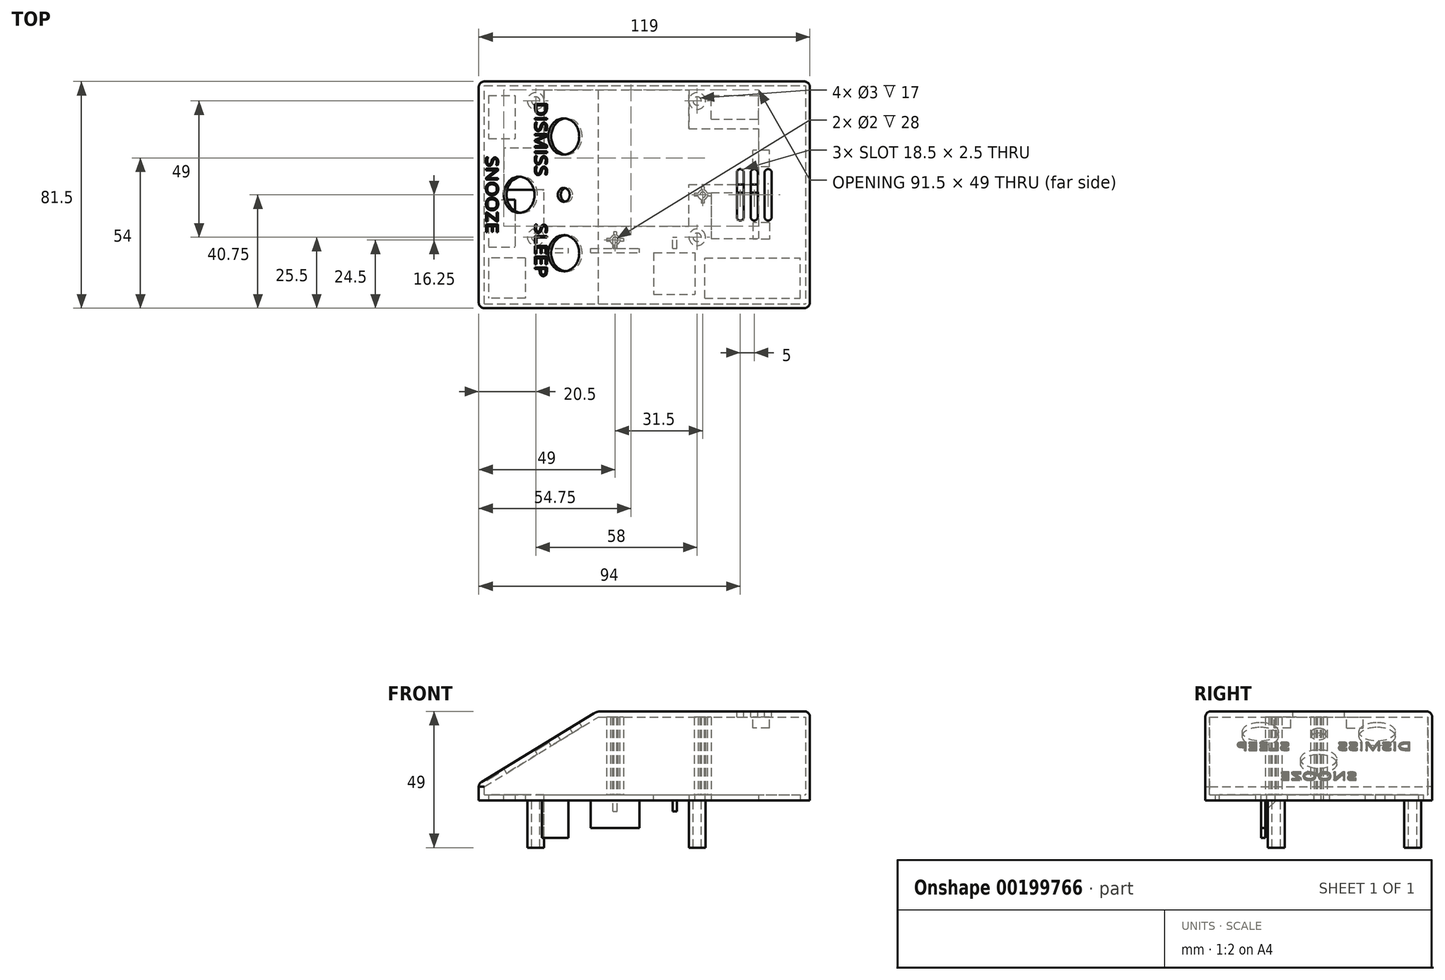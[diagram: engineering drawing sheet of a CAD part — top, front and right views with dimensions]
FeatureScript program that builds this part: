
annotation { "Feature Type Name" : "Feature", "Feature Type Description" : "" }
export const myFeature = defineFeature(function(context is Context, id is Id, definition is map)
    precondition{}
    {
        {
            var Q0;
            Q0=qCreatedBy(makeId("Top.planeOp"),FACE);
            var sketch = newSketch(context, id + "F0", { "sketchPlane" : qUnion([Q0])});
            skLineSegment(sketch, "E0.bottom", {"start": v(0, 0) * mm, "end": v(89, 0) * mm});
            skLineSegment(sketch, "E0.top", {"start": v(0, 60) * mm, "end": v(89, 60) * mm});
            skLineSegment(sketch, "E0.left", {"start": v(0, 0) * mm, "end": v(0, 60) * mm});
            skLineSegment(sketch, "E0.right", {"start": v(89, 0) * mm, "end": v(89, 60) * mm});
            skLineSegment(sketch, "E1", {"start": v(0, 60) * mm, "end": v(-15, 60) * mm});
            skLineSegment(sketch, "E2", {"start": v(-15, 60) * mm, "end": v(-15, 0) * mm});
            skLineSegment(sketch, "E3", {"start": v(-15, 0) * mm, "end": v(-15, -20) * mm});
            skLineSegment(sketch, "E4", {"start": v(-15, -20) * mm, "end": v(89, -20) * mm});
            skLineSegment(sketch, "E5", {"start": v(89, -20) * mm, "end": v(104, -20) * mm});
            skLineSegment(sketch, "E6", {"start": v(104, -20) * mm, "end": v(104, 60) * mm});
            skLineSegment(sketch, "E7", {"start": v(104, 60) * mm, "end": v(89, 60) * mm});
            skLineSegment(sketch, "E8.bottom", {"start": v(-15, 60) * mm, "end": v(104, 60) * mm});
            skLineSegment(sketch, "E8.top", {"start": v(-15, 61.5) * mm, "end": v(104, 61.5) * mm});
            skLineSegment(sketch, "E8.left", {"start": v(-15, 60) * mm, "end": v(-15, 61.5) * mm});
            skLineSegment(sketch, "E8.right", {"start": v(104, 60) * mm, "end": v(104, 61.5) * mm});
            skSolve(sketch);
        }
        {
            var Q0;
            Q0=makeQuery(id+"F0.imprint","IMPRINT",FACE,{"disambiguationData":[TD([[makeQuery(id+"F0.imprint","IMPRINT",EDGE,{"derivedFrom":sQuery(id+"F0.wireOp",EDGE,"E0.bottom")}),-1.0]])]});
            var Q1;
            Q1=makeQuery(id+"F0.imprint","IMPRINT",FACE,{"disambiguationData":[TD([[makeQuery(id+"F0.imprint","IMPRINT",EDGE,{"derivedFrom":sQuery(id+"F0.wireOp",EDGE,"E8.top")}),-1.0]])]});
            var Q2;
            Q2=makeQuery(id+"F0.imprint","IMPRINT",FACE,{"disambiguationData":[TD([[makeQuery(id+"F0.imprint","IMPRINT",EDGE,{"derivedFrom":sQuery(id+"F0.wireOp",EDGE,"E0.bottom")}),1.0]])]});
            extrude(context, id + "F1", {"entities" : qUnion([Q0, Q1, Q2]), "depth" : 2 * mm});
        }
        {
            var Q0;
            Q0=makeQuery(id+"F1.opExtrude","CAP_FACE",FACE,{"disambiguationData":[OSD([sQuery(id+"F0.wireOp",EDGE,"E2"),sQuery(id+"F0.wireOp",EDGE,"E3"),sQuery(id+"F0.wireOp",EDGE,"E4"),sQuery(id+"F0.wireOp",EDGE,"E5"),sQuery(id+"F0.wireOp",EDGE,"E6"),sQuery(id+"F0.wireOp",EDGE,"E8.top"),sQuery(id+"F0.wireOp",EDGE,"E8.left"),sQuery(id+"F0.wireOp",EDGE,"E8.right")])],"isStart":true});
            var sketch = newSketch(context, id + "F2", { "sketchPlane" : qUnion([Q0])});
            skCircle(sketch, "E9", {"center": v(5.5, -5.5) * mm, "radius": 1.5 * mm});
            skCircle(sketch, "E10.0", {"center": v(5.5, -5.5) * mm, "radius": 3 * mm});
            skCircle(sketch, "E11.0.1.0", {"center": v(5.5, -54.5) * mm, "radius": 3 * mm});
            skCircle(sketch, "E11.0.1.1", {"center": v(5.5, -54.5) * mm, "radius": 1.5 * mm});
            skCircle(sketch, "E11.1.0.0", {"center": v(63.5, -5.5) * mm, "radius": 3 * mm});
            skCircle(sketch, "E11.1.0.1", {"center": v(63.5, -5.5) * mm, "radius": 1.5 * mm});
            skCircle(sketch, "E11.1.1.0", {"center": v(63.5, -54.5) * mm, "radius": 3 * mm});
            skCircle(sketch, "E11.1.1.1", {"center": v(63.5, -54.5) * mm, "radius": 1.5 * mm});
            skLineSegment(sketch, "E11.direction1", {"start": v(5.5, -5.5) * mm, "end": v(63.5, -5.5) * mm, "construction": true});
            skLineSegment(sketch, "E11.direction2", {"start": v(5.5, -5.5) * mm, "end": v(5.5, -54.5) * mm, "construction": true});
            skSolve(sketch);
        }
        {
            var Q0;
            Q0=makeQuery(id+"F2.imprint","IMPRINT",FACE,{"disambiguationData":[TD([[makeQuery(id+"F2.imprint","IMPRINT",EDGE,{"derivedFrom":sQuery(id+"F2.wireOp",EDGE,"E9")}),-1.0]])]});
            var Q1;
            Q1=makeQuery(id+"F2.imprint","IMPRINT",FACE,{"disambiguationData":[TD([[makeQuery(id+"F2.imprint","IMPRINT",EDGE,{"derivedFrom":sQuery(id+"F2.wireOp",EDGE,"E11.1.0.0")}),1.0]])]});
            var Q2;
            Q2=makeQuery(id+"F2.imprint","IMPRINT",FACE,{"disambiguationData":[TD([[makeQuery(id+"F2.imprint","IMPRINT",EDGE,{"derivedFrom":sQuery(id+"F2.wireOp",EDGE,"E11.0.1.0")}),1.0]])]});
            var Q3;
            Q3=makeQuery(id+"F2.imprint","IMPRINT",FACE,{"disambiguationData":[TD([[makeQuery(id+"F2.imprint","IMPRINT",EDGE,{"derivedFrom":sQuery(id+"F2.wireOp",EDGE,"E11.1.1.0")}),1.0]])]});
            extrude(context, id + "F3", {"entities" : qUnion([Q0, Q1, Q2, Q3]), "operationType" : NewBodyOperationType.ADD, "depth" : 17 * mm});
        }
        {
            var Q0;
            Q0=makeQuery(id+"F1.opExtrude","CAP_FACE",FACE,{"disambiguationData":[OSD([sQuery(id+"F0.wireOp",EDGE,"E2"),sQuery(id+"F0.wireOp",EDGE,"E3"),sQuery(id+"F0.wireOp",EDGE,"E4"),sQuery(id+"F0.wireOp",EDGE,"E5"),sQuery(id+"F0.wireOp",EDGE,"E6"),sQuery(id+"F0.wireOp",EDGE,"E8.top"),sQuery(id+"F0.wireOp",EDGE,"E8.left"),sQuery(id+"F0.wireOp",EDGE,"E8.right")])],"isStart":false});
            var sketch = newSketch(context, id + "F4", { "sketchPlane" : qUnion([Q0])});
            skLineSegment(sketch, "E12.bottom", {"start": v(8.5, 9.5) * mm, "end": v(60.5, 9.5) * mm});
            skLineSegment(sketch, "E12.top", {"start": v(8.5, 58.5) * mm, "end": v(60.5, 58.5) * mm});
            skLineSegment(sketch, "E12.left", {"start": v(8.5, 9.5) * mm, "end": v(8.5, 58.5) * mm});
            skLineSegment(sketch, "E12.right", {"start": v(60.5, 9.5) * mm, "end": v(60.5, 58.5) * mm});
            skLineSegment(sketch, "E13.bottom", {"start": v(0, 0) * mm, "end": v(89, 0) * mm});
            skLineSegment(sketch, "E13.top", {"start": v(0, 60) * mm, "end": v(89, 60) * mm});
            skLineSegment(sketch, "E13.left", {"start": v(0, 0) * mm, "end": v(0, 60) * mm});
            skLineSegment(sketch, "E13.right", {"start": v(89, 0) * mm, "end": v(89, 60) * mm});
            skSolve(sketch);
        }
        {
            var Q0;
            Q0=makeQuery(id+"F4.imprint","IMPRINT",FACE,{"disambiguationData":[TD([[makeQuery(id+"F4.imprint","IMPRINT",EDGE,{"derivedFrom":sQuery(id+"F4.wireOp",EDGE,"E12.bottom")}),1.0]])]});
            var Q1;
            {var subQ0=sQuery(id+"F0.wireOp",EDGE,"E8.top");var subQ1=sQuery(id+"F0.wireOp",EDGE,"E8.right");var subQ2=sQuery(id+"F0.wireOp",EDGE,"E6");var subQ3=sQuery(id+"F0.wireOp",EDGE,"E5");var subQ4=sQuery(id+"F0.wireOp",EDGE,"E4");var subQ5=sQuery(id+"F0.wireOp",EDGE,"E8.left");var subQ6=sQuery(id+"F0.wireOp",EDGE,"E3");var subQ7=sQuery(id+"F0.wireOp",EDGE,"E2");Q1=makeQuery(id+"F3.boolean.opBoolean","SPLIT",FACE,{"disambiguationData":[TD([makeQuery(id+"F1.opExtrude","SWEPT_FACE",FACE,{"disambiguationData":[OSD([subQ0])]})])],"derivedFrom":makeQuery(id+"F1.opExtrude","CAP_FACE",FACE,{"disambiguationData":[OSD([subQ7,subQ6,subQ4,subQ3,subQ2,subQ0,subQ5,subQ1])],"isStart":true})});}
            extrude(context, id + "F5", {"entities" : qUnion([Q0]), "operationType" : NewBodyOperationType.REMOVE, "endBound" : BoundingType.UP_TO_SURFACE, "oppositeDirection" : true, "endBoundEntityFace" : qUnion([Q1]), "depth" : 25 * mm});
        }
        {
            var Q0;
            Q0=makeQuery(id+"F1.opExtrude","CAP_FACE",FACE,{"disambiguationData":[OSD([sQuery(id+"F0.wireOp",EDGE,"E2"),sQuery(id+"F0.wireOp",EDGE,"E3"),sQuery(id+"F0.wireOp",EDGE,"E4"),sQuery(id+"F0.wireOp",EDGE,"E5"),sQuery(id+"F0.wireOp",EDGE,"E6"),sQuery(id+"F0.wireOp",EDGE,"E8.top"),sQuery(id+"F0.wireOp",EDGE,"E8.left"),sQuery(id+"F0.wireOp",EDGE,"E8.right")])],"isStart":false});
            var sketch = newSketch(context, id + "F6", { "sketchPlane" : qUnion([Q0])});
            skLineSegment(sketch, "E14.bottom", {"start": v(104, 61.5) * mm, "end": v(102.5, 61.5) * mm});
            skLineSegment(sketch, "E14.top", {"start": v(104, -20) * mm, "end": v(102.5, -20) * mm});
            skLineSegment(sketch, "E14.left", {"start": v(104, 61.5) * mm, "end": v(104, -20) * mm});
            skLineSegment(sketch, "E14.right", {"start": v(102.5, 61.5) * mm, "end": v(102.5, -20) * mm});
            skSolve(sketch);
        }
        {
            var Q0;
            Q0=makeQuery(id+"F6.imprint","IMPRINT",FACE,{"disambiguationData":[TD([[makeQuery(id+"F6.imprint","IMPRINT",EDGE,{"derivedFrom":sQuery(id+"F6.wireOp",EDGE,"E14.bottom")}),-1.0]])]});
            extrude(context, id + "F7", {"entities" : qUnion([Q0]), "operationType" : NewBodyOperationType.ADD, "depth" : 30 * mm});
        }
        {
            var Q0;
            Q0=makeQuery(id+"F1.opExtrude","CAP_FACE",FACE,{"disambiguationData":[OSD([sQuery(id+"F0.wireOp",EDGE,"E2"),sQuery(id+"F0.wireOp",EDGE,"E3"),sQuery(id+"F0.wireOp",EDGE,"E4"),sQuery(id+"F0.wireOp",EDGE,"E5"),sQuery(id+"F0.wireOp",EDGE,"E6"),sQuery(id+"F0.wireOp",EDGE,"E8.top"),sQuery(id+"F0.wireOp",EDGE,"E8.left"),sQuery(id+"F0.wireOp",EDGE,"E8.right")])],"isStart":false});
            var sketch = newSketch(context, id + "F8", { "sketchPlane" : qUnion([Q0])});
            skLineSegment(sketch, "E15.bottom", {"start": v(8.5, 37.5) * mm, "end": v(-6, 37.5) * mm});
            skLineSegment(sketch, "E15.top", {"start": v(8.5, 22.5) * mm, "end": v(-6, 22.5) * mm});
            skLineSegment(sketch, "E15.left", {"start": v(8.5, 37.5) * mm, "end": v(8.5, 22.5) * mm});
            skLineSegment(sketch, "E15.right", {"start": v(-6, 37.5) * mm, "end": v(-6, 22.5) * mm});
            skLineSegment(sketch, "E16.bottom", {"start": v(8.5, 22.5) * mm, "end": v(1.5, 22.5) * mm});
            skLineSegment(sketch, "E16.top", {"start": v(8.5, 9.5) * mm, "end": v(1.5, 9.5) * mm});
            skLineSegment(sketch, "E16.left", {"start": v(8.5, 22.5) * mm, "end": v(8.5, 9.5) * mm});
            skLineSegment(sketch, "E16.right", {"start": v(1.5, 22.5) * mm, "end": v(1.5, 9.5) * mm});
            skSolve(sketch);
        }
        {
            var Q0;
            Q0=makeQuery(id+"F8.imprint","IMPRINT",FACE,{"disambiguationData":[TD([[makeQuery(id+"F8.imprint","IMPRINT",EDGE,{"derivedFrom":sQuery(id+"F8.wireOp",EDGE,"E15.bottom")}),1.0]])]});
            var Q1;
            Q1=makeQuery(id+"F8.imprint","IMPRINT",FACE,{"disambiguationData":[TD([[makeQuery(id+"F8.imprint","IMPRINT",EDGE,{"derivedFrom":sQuery(id+"F8.wireOp",EDGE,"E16.bottom")}),1.0]])]});
            var Q2;
            {var subQ0=sQuery(id+"F0.wireOp",EDGE,"E8.top");var subQ1=sQuery(id+"F0.wireOp",EDGE,"E8.right");var subQ2=sQuery(id+"F0.wireOp",EDGE,"E6");var subQ3=sQuery(id+"F0.wireOp",EDGE,"E5");var subQ4=sQuery(id+"F0.wireOp",EDGE,"E4");var subQ5=sQuery(id+"F0.wireOp",EDGE,"E8.left");var subQ6=sQuery(id+"F0.wireOp",EDGE,"E3");var subQ7=sQuery(id+"F0.wireOp",EDGE,"E2");Q2=makeQuery(id+"F3.boolean.opBoolean","SPLIT",FACE,{"disambiguationData":[TD([makeQuery(id+"F1.opExtrude","SWEPT_FACE",FACE,{"disambiguationData":[OSD([subQ0])]})])],"derivedFrom":makeQuery(id+"F1.opExtrude","CAP_FACE",FACE,{"disambiguationData":[OSD([subQ7,subQ6,subQ4,subQ3,subQ2,subQ0,subQ5,subQ1])],"isStart":true})});}
            extrude(context, id + "F9", {"entities" : qUnion([Q0, Q1]), "operationType" : NewBodyOperationType.REMOVE, "endBound" : BoundingType.UP_TO_SURFACE, "oppositeDirection" : true, "endBoundEntityFace" : qUnion([Q2]), "depth" : 25 * mm});
        }
        {
            var Q0;
            Q0=makeQuery(id+"F7.boolean.opBoolean","MERGE",FACE,{"derivedFrom":[makeQuery(id+"F1.opExtrude","SWEPT_FACE",FACE,{"disambiguationData":[OSD([sQuery(id+"F0.wireOp",EDGE,"E8.top")])]}),makeQuery(id+"F7.opExtrude","SWEPT_FACE",FACE,{"disambiguationData":[OSD([sQuery(id+"F6.wireOp",EDGE,"E14.bottom")])]})]});
            var sketch = newSketch(context, id + "F10", { "sketchPlane" : qUnion([Q0])});
            skLineSegment(sketch, "E17", {"start": v(15, 2) * mm, "end": v(15, 6) * mm});
            skLineSegment(sketch, "E18", {"start": v(15, 6) * mm, "end": v(-27.5, 32) * mm});
            skLineSegment(sketch, "E19", {"start": v(-27.5, 32) * mm, "end": v(-102.5, 32) * mm});
            skSolve(sketch);
        }
        {
            var Q0;
            Q0=makeQuery(id+"F10.imprint","IMPRINT",FACE,{"disambiguationData":[TD([[makeQuery(id+"F10.imprint","IMPRINT",EDGE,{"derivedFrom":sQuery(id+"F10.wireOp",EDGE,"E17")}),1.0]])]});
            extrude(context, id + "F11", {"entities" : qUnion([Q0]), "operationType" : NewBodyOperationType.ADD, "oppositeDirection" : true, "depth" : 1.5 * mm});
        }
        {
            var Q0;
            Q0=makeQuery(id+"F7.boolean.opBoolean","MERGE",FACE,{"derivedFrom":[makeQuery(id+"F1.opExtrude","SWEPT_FACE",FACE,{"disambiguationData":[OSD([sQuery(id+"F0.wireOp",EDGE,"E4"),sQuery(id+"F0.wireOp",EDGE,"E5")])]}),makeQuery(id+"F7.opExtrude","SWEPT_FACE",FACE,{"disambiguationData":[OSD([sQuery(id+"F6.wireOp",EDGE,"E14.top")])]})]});
            var sketch = newSketch(context, id + "F12", { "sketchPlane" : qUnion([Q0])});
            skLineSegment(sketch, "E20.0.0", {"start": v(104, 0) * mm, "end": v(-15, 0) * mm});
            skLineSegment(sketch, "E20.0.1", {"start": v(-15, 0) * mm, "end": v(-15, 6) * mm});
            skLineSegment(sketch, "E20.0.2", {"start": v(-15, 6) * mm, "end": v(27.5, 32) * mm});
            skLineSegment(sketch, "E20.0.3", {"start": v(27.5, 32) * mm, "end": v(104, 32) * mm});
            skLineSegment(sketch, "E20.0.4", {"start": v(104, 32) * mm, "end": v(104, 0) * mm});
            skSolve(sketch);
        }
        {
            var Q0;
            {var subQ4=sQuery(id+"F12.wireOp",EDGE,"E20.0.2");Q0=makeQuery(id+"F12.imprint","IMPRINT",FACE,{"disambiguationData":[TD([[makeQuery(id+"F12.imprint","IMPRINT",EDGE,{"derivedFrom":subQ4}),-1.0]])]});}
            extrude(context, id + "F13", {"entities" : qUnion([Q0]), "operationType" : NewBodyOperationType.ADD, "oppositeDirection" : true, "depth" : 1.5 * mm});
        }
        {
            var Q0;
            Q0=makeQuery(id+"F1.opExtrude","CAP_FACE",FACE,{"disambiguationData":[OSD([sQuery(id+"F0.wireOp",EDGE,"E2"),sQuery(id+"F0.wireOp",EDGE,"E3"),sQuery(id+"F0.wireOp",EDGE,"E4"),sQuery(id+"F0.wireOp",EDGE,"E5"),sQuery(id+"F0.wireOp",EDGE,"E6"),sQuery(id+"F0.wireOp",EDGE,"E8.top"),sQuery(id+"F0.wireOp",EDGE,"E8.left"),sQuery(id+"F0.wireOp",EDGE,"E8.right")])],"isStart":false});
            var sketch = newSketch(context, id + "F14", { "sketchPlane" : qUnion([Q0])});
            skLineSegment(sketch, "E21.bottom", {"start": v(47.88, 0) * mm, "end": v(62.69, 0) * mm});
            skLineSegment(sketch, "E21.top", {"start": v(47.88, -15) * mm, "end": v(62.69, -15) * mm});
            skLineSegment(sketch, "E21.left", {"start": v(47.88, 0) * mm, "end": v(47.88, -15) * mm});
            skLineSegment(sketch, "E21.right", {"start": v(62.69, 0) * mm, "end": v(62.69, -15) * mm});
            skSolve(sketch);
        }
        {
            var Q0;
            Q0=makeQuery(id+"F14.imprint","IMPRINT",FACE,{"disambiguationData":[TD([[makeQuery(id+"F14.imprint","IMPRINT",EDGE,{"derivedFrom":sQuery(id+"F14.wireOp",EDGE,"E21.bottom")}),-1.0]])]});
            extrude(context, id + "F15", {"entities" : qUnion([Q0]), "operationType" : NewBodyOperationType.REMOVE, "endBound" : BoundingType.UP_TO_NEXT, "oppositeDirection" : true, "depth" : 25 * mm});
        }
        {
            var Q0;
            Q0=makeQuery(id+"F11.opExtrude","CAP_FACE",FACE,{"disambiguationData":[OSD([sQuery(id+"F0.wireOp",EDGE,"E8.top"),sQuery(id+"F6.wireOp",EDGE,"E14.bottom"),sQuery(id+"F6.wireOp",EDGE,"E14.right"),sQuery(id+"F10.wireOp",EDGE,"E17"),sQuery(id+"F10.wireOp",EDGE,"E18"),sQuery(id+"F10.wireOp",EDGE,"E19")])],"isStart":false});
            var sketch = newSketch(context, id + "F16", { "sketchPlane" : qUnion([Q0])});
            skLineSegment(sketch, "E22", {"start": v(-13, 2) * mm, "end": v(-13, 4.88) * mm});
            skLineSegment(sketch, "E23", {"start": v(-13, 4.88) * mm, "end": v(28.06, 30) * mm});
            skLineSegment(sketch, "E24", {"start": v(28.06, 30) * mm, "end": v(102.5, 30) * mm});
            skSolve(sketch);
        }
        {
            var Q0;
            {var subQ5=sQuery(id+"F16.wireOp",EDGE,"E22");Q0=makeQuery(id+"F16.imprint","IMPRINT",FACE,{"disambiguationData":[TD([[makeQuery(id+"F16.imprint","IMPRINT",EDGE,{"derivedFrom":subQ5}),1.0]])]});}
            var Q1;
            Q1=makeQuery(id+"F13.opExtrude","CAP_FACE",FACE,{"disambiguationData":[OSD([sQuery(id+"F0.wireOp",EDGE,"E4"),sQuery(id+"F0.wireOp",EDGE,"E5"),sQuery(id+"F6.wireOp",EDGE,"E14.top"),sQuery(id+"F6.wireOp",EDGE,"E14.right"),sQuery(id+"F12.wireOp",EDGE,"E20.0.1"),sQuery(id+"F12.wireOp",EDGE,"E20.0.2"),sQuery(id+"F12.wireOp",EDGE,"E20.0.3")])],"isStart":false});
            extrude(context, id + "F17", {"entities" : qUnion([Q0]), "operationType" : NewBodyOperationType.ADD, "endBound" : BoundingType.UP_TO_SURFACE, "endBoundEntityFace" : qUnion([Q1]), "depth" : 25 * mm});
        }
        {
            var Q0;
            {var subQ0=sQuery(id+"F10.wireOp",EDGE,"E18");Q0=makeQuery(id+"F17.boolean.opBoolean","MERGE",FACE,{"derivedFrom":[makeQuery(id+"F11.opExtrude","SWEPT_FACE",FACE,{"disambiguationData":[OSD([subQ0])]}),makeQuery(id+"F13.opExtrude","SWEPT_FACE",FACE,{"disambiguationData":[OSD([sQuery(id+"F12.wireOp",EDGE,"E20.0.2")])]}),makeQuery(id+"F17.opExtrude","SWEPT_FACE",FACE,{"disambiguationData":[OSD([subQ0])]})]});}
            var sketch = newSketch(context, id + "F18", { "sketchPlane" : qUnion([Q0])});
            skCircle(sketch, "E25", {"center": v(7.34, 20.75) * mm, "radius": 6.5 * mm});
            skPoint(sketch, "E25.centerSnap0", {"position": v(-9.66, 20.75) * mm});
            skCircle(sketch, "E26", {"center": v(26.16, -0.25) * mm, "radius": 6.5 * mm});
            skCircle(sketch, "E27", {"center": v(26.16, 41.75) * mm, "radius": 6.5 * mm});
            skLineSegment(sketch, "E28", {"start": v(26.16, 41.75) * mm, "end": v(40.16, 41.75) * mm});
            skLineSegment(sketch, "E29", {"start": v(26.16, -0.25) * mm, "end": v(40.16, -0.25) * mm});
            skLineSegment(sketch, "E30", {"start": v(40.16, 41.75) * mm, "end": v(40.16, 20.75) * mm});
            skLineSegment(sketch, "E31", {"start": v(40.16, 20.75) * mm, "end": v(40.16, -0.25) * mm});
            skSolve(sketch);
        }
        {
            var Q0;
            Q0=makeQuery(id+"F18.imprint","IMPRINT",FACE,{"disambiguationData":[TD([[makeQuery(id+"F18.imprint","IMPRINT",EDGE,{"derivedFrom":sQuery(id+"F18.wireOp",EDGE,"E25")}),1.0]])]});
            var Q1;
            Q1=makeQuery(id+"F18.imprint","IMPRINT",FACE,{"disambiguationData":[TD([[makeQuery(id+"F18.imprint","IMPRINT",EDGE,{"derivedFrom":sQuery(id+"F18.wireOp",EDGE,"E27")}),1.0]])]});
            var Q2;
            Q2=makeQuery(id+"F18.imprint","IMPRINT",FACE,{"disambiguationData":[TD([[makeQuery(id+"F18.imprint","IMPRINT",EDGE,{"derivedFrom":sQuery(id+"F18.wireOp",EDGE,"E26")}),1.0]])]});
            extrude(context, id + "F19", {"entities" : qUnion([Q0, Q1, Q2]), "operationType" : NewBodyOperationType.REMOVE, "endBound" : BoundingType.UP_TO_NEXT, "oppositeDirection" : true, "depth" : 25 * mm});
        }
        {
            var Q0;
            {var subQ0=sQuery(id+"F10.wireOp",EDGE,"E18");Q0=makeQuery(id+"F17.boolean.opBoolean","MERGE",FACE,{"derivedFrom":[makeQuery(id+"F11.opExtrude","SWEPT_FACE",FACE,{"disambiguationData":[OSD([subQ0])]}),makeQuery(id+"F13.opExtrude","SWEPT_FACE",FACE,{"disambiguationData":[OSD([sQuery(id+"F12.wireOp",EDGE,"E20.0.2")])]}),makeQuery(id+"F17.opExtrude","SWEPT_FACE",FACE,{"disambiguationData":[OSD([subQ0])]})]});}
            var sketch = newSketch(context, id + "F20", { "sketchPlane" : qUnion([Q0])});
            skCircle(sketch, "E32.0", {"center": v(26.16, 41.75) * mm, "radius": 6.5 * mm});
            skCircle(sketch, "E33.0", {"center": v(26.16, -0.25) * mm, "radius": 6.5 * mm});
            skCircle(sketch, "E34.0", {"center": v(7.34, 20.75) * mm, "radius": 6.5 * mm});
            skCircle(sketch, "E35", {"center": v(26.16, 20.75) * mm, "radius": 2.5 * mm});
            skSolve(sketch);
        }
        {
            var Q0;
            Q0=makeQuery(id+"F20.imprint","IMPRINT",FACE,{"disambiguationData":[TD([[makeQuery(id+"F20.imprint","IMPRINT",EDGE,{"derivedFrom":sQuery(id+"F20.wireOp",EDGE,"E35")}),1.0]])]});
            extrude(context, id + "F21", {"entities" : qUnion([Q0]), "operationType" : NewBodyOperationType.REMOVE, "endBound" : BoundingType.UP_TO_NEXT, "oppositeDirection" : true, "depth" : 25 * mm});
        }
        {
            var Q0;
            {var subQ0=sQuery(id+"F10.wireOp",EDGE,"E18");Q0=makeQuery(id+"F17.boolean.opBoolean","MERGE",FACE,{"derivedFrom":[makeQuery(id+"F11.opExtrude","SWEPT_FACE",FACE,{"disambiguationData":[OSD([subQ0])]}),makeQuery(id+"F13.opExtrude","SWEPT_FACE",FACE,{"disambiguationData":[OSD([sQuery(id+"F12.wireOp",EDGE,"E20.0.2")])]}),makeQuery(id+"F17.opExtrude","SWEPT_FACE",FACE,{"disambiguationData":[OSD([subQ0])]})]});}
            var sketch = newSketch(context, id + "F22", { "sketchPlane" : qUnion([Q0])});
            skText(sketch, "E36", { "text": "SNOOZE", "fontName": "OpenSans-Regular.ttf"});
            skLineSegment(sketch, "E37", {"start": v(-7.16, 34.61) * mm, "end": v(-7.16, 61.5) * mm});
            skLineSegment(sketch, "E38", {"start": v(-7.16, 6.89) * mm, "end": v(-7.16, -20) * mm});
            skLineSegment(sketch, "E39", {"start": v(7.34, 20.75) * mm, "end": v(0.34, 20.75) * mm});
            skLineSegment(sketch, "E40", {"start": v(-2.16, 20.75) * mm, "end": v(0.34, 20.75) * mm});
            skLineSegment(sketch, "E41", {"start": v(-7.16, 20.75) * mm, "end": v(-9.66, 20.75) * mm});
            skText(sketch, "E42", { "text": "DISMISS\n", "fontName": "OpenSans-Regular.ttf"});
            skLineSegment(sketch, "E43", {"start": v(26.16, 41.75) * mm, "end": v(19.16, 41.75) * mm});
            skLineSegment(sketch, "E44", {"start": v(17.16, 41.75) * mm, "end": v(19.16, 41.75) * mm});
            skText(sketch, "E45", { "text": "SLEEP", "fontName": "OpenSans-Regular.ttf"});
            skLineSegment(sketch, "E46", {"start": v(26.16, -0.25) * mm, "end": v(19.16, -0.25) * mm});
            skLineSegment(sketch, "E47", {"start": v(17.16, -0.25) * mm, "end": v(19.16, -0.25) * mm});
            const initialGuessF22  = {"E36": [-0.00658, 0.03461, 0, -1, 0.005], "E42": [0.01402, 0.05413, 0, -1, 0.005], "E45": [0.01402, 0.01046, 0, -1, 0.005]};
            skSetInitialGuess(sketch, initialGuessF22);
            skSolve(sketch);
        }
        {
            var Q0;
            Q0=qSketchRegion(id+"F22",true);
            extrude(context, id + "F23", {"entities" : qUnion([Q0]), "operationType" : NewBodyOperationType.REMOVE, "oppositeDirection" : true, "depth" : 0.5 * mm});
        }
        {
            var Q0;
            {var subQ0=sQuery(id+"F10.wireOp",EDGE,"E19");var subQ1=sQuery(id+"F10.wireOp",EDGE,"E18");Q0=makeQuery(id+"F17.boolean.opBoolean","MERGE",EDGE,{"derivedFrom":[makeQuery(id+"F11.opExtrude","SWEPT_EDGE",EDGE,{"disambiguationData":[OSD([subQ1,subQ0])]}),makeQuery(id+"F13.opExtrude","SWEPT_EDGE",EDGE,{"disambiguationData":[OSD([sQuery(id+"F12.wireOp",EDGE,"E20.0.2"),sQuery(id+"F12.wireOp",EDGE,"E20.0.3")])]}),makeQuery(id+"F17.opExtrude","SWEPT_EDGE",EDGE,{"disambiguationData":[OSD([subQ1,subQ0])]})]});}
            fillet(context, id + "F24", {"entities" : qUnion([Q0]), "radius" : 5 * mm, "tangentPropagation" : true, "allowEdgeOverflow" : false});
        }
        {
            var Q0;
            {var subQ0=sQuery(id+"F10.wireOp",EDGE,"E19");Q0=makeQuery(id+"F17.boolean.opBoolean","MERGE",FACE,{"derivedFrom":[makeQuery(id+"F13.boolean.opBoolean","MERGE",FACE,{"derivedFrom":[makeQuery(id+"F11.boolean.opBoolean","MERGE",FACE,{"derivedFrom":[makeQuery(id+"F7.opExtrude","CAP_FACE",FACE,{"disambiguationData":[OSD([sQuery(id+"F6.wireOp",EDGE,"E14.bottom"),sQuery(id+"F6.wireOp",EDGE,"E14.top"),sQuery(id+"F6.wireOp",EDGE,"E14.left"),sQuery(id+"F6.wireOp",EDGE,"E14.right")])],"isStart":false}),makeQuery(id+"F11.opExtrude","SWEPT_FACE",FACE,{"disambiguationData":[OSD([subQ0])]})]}),makeQuery(id+"F13.opExtrude","SWEPT_FACE",FACE,{"disambiguationData":[OSD([sQuery(id+"F12.wireOp",EDGE,"E20.0.3")])]})]}),makeQuery(id+"F17.opExtrude","SWEPT_FACE",FACE,{"disambiguationData":[OSD([subQ0])]})]});}
            var sketch = newSketch(context, id + "F25", { "sketchPlane" : qUnion([Q0])});
            skLineSegment(sketch, "E48", {"start": v(79, 28.75) * mm, "end": v(79, 12.75) * mm});
            skLineSegment(sketch, "E49", {"start": v(79, 28.75) * mm, "end": v(79, 61.5) * mm});
            skLineSegment(sketch, "E50", {"start": v(79, 12.75) * mm, "end": v(79, -20) * mm});
            skArc(sketch, "E51.0.startCap", {"start": v(77.75, 28.75) * mm, "mid": v(79, 30) * mm, "end": v(80.25, 28.75) * mm});
            skArc(sketch, "E51.0.endCap", {"start": v(80.25, 12.75) * mm, "mid": v(79, 11.5) * mm, "end": v(77.75, 12.75) * mm});
            skLineSegment(sketch, "E51.0.left", {"start": v(80.25, 28.75) * mm, "end": v(80.25, 12.75) * mm});
            skLineSegment(sketch, "E51.0.right", {"start": v(77.75, 28.75) * mm, "end": v(77.75, 12.75) * mm});
            skLineSegment(sketch, "E52.1.0.0", {"start": v(85.25, 28.75) * mm, "end": v(85.25, 12.75) * mm});
            skLineSegment(sketch, "E52.1.0.1", {"start": v(82.75, 28.75) * mm, "end": v(82.75, 12.75) * mm});
            skArc(sketch, "E52.1.0.2", {"start": v(82.75, 28.75) * mm, "mid": v(84, 30) * mm, "end": v(85.25, 28.75) * mm});
            skArc(sketch, "E52.1.0.3", {"start": v(85.25, 12.75) * mm, "mid": v(84, 11.5) * mm, "end": v(82.75, 12.75) * mm});
            skLineSegment(sketch, "E52.2.0.0", {"start": v(90.25, 28.75) * mm, "end": v(90.25, 12.75) * mm});
            skLineSegment(sketch, "E52.2.0.1", {"start": v(87.75, 28.75) * mm, "end": v(87.75, 12.75) * mm});
            skArc(sketch, "E52.2.0.2", {"start": v(87.75, 28.75) * mm, "mid": v(89, 30) * mm, "end": v(90.25, 28.75) * mm});
            skArc(sketch, "E52.2.0.3", {"start": v(90.25, 12.75) * mm, "mid": v(89, 11.5) * mm, "end": v(87.75, 12.75) * mm});
            skLineSegment(sketch, "E52.direction1", {"start": v(80.25, 12.75) * mm, "end": v(85.25, 12.75) * mm, "construction": true});
            skSolve(sketch);
        }
        {
            var Q0;
            {var subQ1=sQuery(id+"F25.wireOp",EDGE,"E48");Q0=makeQuery(id+"F25.imprint","IMPRINT",FACE,{"disambiguationData":[TD([[makeQuery(id+"F25.imprint","IMPRINT",EDGE,{"derivedFrom":subQ1}),-1.0]])]});}
            var Q1;
            {var subQ5=sQuery(id+"F25.wireOp",EDGE,"E48");Q1=makeQuery(id+"F25.imprint","IMPRINT",FACE,{"disambiguationData":[TD([[makeQuery(id+"F25.imprint","IMPRINT",EDGE,{"derivedFrom":subQ5}),1.0]])]});}
            var Q2;
            Q2=makeQuery(id+"F25.imprint","IMPRINT",FACE,{"disambiguationData":[TD([[makeQuery(id+"F25.imprint","IMPRINT",EDGE,{"derivedFrom":sQuery(id+"F25.wireOp",EDGE,"E52.1.0.0")}),-1.0]])]});
            var Q3;
            Q3=makeQuery(id+"F25.imprint","IMPRINT",FACE,{"disambiguationData":[TD([[makeQuery(id+"F25.imprint","IMPRINT",EDGE,{"derivedFrom":sQuery(id+"F25.wireOp",EDGE,"E52.2.0.0")}),-1.0]])]});
            extrude(context, id + "F26", {"entities" : qUnion([Q0, Q1, Q2, Q3]), "operationType" : NewBodyOperationType.REMOVE, "endBound" : BoundingType.UP_TO_NEXT, "oppositeDirection" : true, "depth" : 25 * mm});
        }
        {
            var Q0;
            Q0=makeQuery(id+"F13.boolean.opBoolean","MERGE",EDGE,{"derivedFrom":[makeQuery(id+"F1.opExtrude","SWEPT_EDGE",EDGE,{"disambiguationData":[OSD([sQuery(id+"F0.wireOp",EDGE,"E3"),sQuery(id+"F0.wireOp",EDGE,"E4")])]}),makeQuery(id+"F13.opExtrude","CAP_EDGE",EDGE,{"disambiguationData":[OSD([sQuery(id+"F12.wireOp",EDGE,"E20.0.1")])],"isStart":true})]});
            var Q1;
            Q1=makeQuery(id+"F11.boolean.opBoolean","MERGE",EDGE,{"derivedFrom":[makeQuery(id+"F1.opExtrude","SWEPT_EDGE",EDGE,{"disambiguationData":[OSD([sQuery(id+"F0.wireOp",EDGE,"E8.top"),sQuery(id+"F0.wireOp",EDGE,"E8.left")])]}),makeQuery(id+"F11.opExtrude","CAP_EDGE",EDGE,{"disambiguationData":[OSD([sQuery(id+"F10.wireOp",EDGE,"E17")])],"isStart":true})]});
            var Q2;
            Q2=makeQuery(id+"F7.boolean.opBoolean","MERGE",EDGE,{"derivedFrom":[makeQuery(id+"F1.opExtrude","SWEPT_EDGE",EDGE,{"disambiguationData":[OSD([sQuery(id+"F0.wireOp",EDGE,"E5"),sQuery(id+"F0.wireOp",EDGE,"E6")])]}),makeQuery(id+"F7.opExtrude","SWEPT_EDGE",EDGE,{"disambiguationData":[OSD([sQuery(id+"F6.wireOp",EDGE,"E14.top"),sQuery(id+"F6.wireOp",EDGE,"E14.left")])]})]});
            var Q3;
            Q3=makeQuery(id+"F7.boolean.opBoolean","MERGE",EDGE,{"derivedFrom":[makeQuery(id+"F1.opExtrude","SWEPT_EDGE",EDGE,{"disambiguationData":[OSD([sQuery(id+"F0.wireOp",EDGE,"E8.top"),sQuery(id+"F0.wireOp",EDGE,"E8.right")])]}),makeQuery(id+"F7.opExtrude","SWEPT_EDGE",EDGE,{"disambiguationData":[OSD([sQuery(id+"F6.wireOp",EDGE,"E14.bottom"),sQuery(id+"F6.wireOp",EDGE,"E14.left")])]})]});
            fillet(context, id + "F27", {"entities" : qUnion([Q0, Q1, Q2, Q3]), "radius" : 2 * mm, "tangentPropagation" : true, "allowEdgeOverflow" : false});
        }
        {
            var Q0;
            Q0=makeQuery(id+"F13.opExtrude","CAP_EDGE",EDGE,{"disambiguationData":[OSD([sQuery(id+"F12.wireOp",EDGE,"E20.0.2")])],"isStart":true});
            fillet(context, id + "F28", {"entities" : qUnion([Q0]), "radius" : 2 * mm, "tangentPropagation" : true, "allowEdgeOverflow" : false});
        }
        {
            var Q0;
            {var subQ0=sQuery(id+"F0.wireOp",EDGE,"E8.top");var subQ1=sQuery(id+"F0.wireOp",EDGE,"E8.right");var subQ2=sQuery(id+"F0.wireOp",EDGE,"E6");var subQ3=sQuery(id+"F0.wireOp",EDGE,"E5");var subQ4=sQuery(id+"F0.wireOp",EDGE,"E4");var subQ5=sQuery(id+"F0.wireOp",EDGE,"E8.left");var subQ6=sQuery(id+"F0.wireOp",EDGE,"E3");var subQ7=sQuery(id+"F0.wireOp",EDGE,"E2");Q0=makeQuery(id+"F3.boolean.opBoolean","SPLIT",FACE,{"disambiguationData":[TD([makeQuery(id+"F1.opExtrude","SWEPT_FACE",FACE,{"disambiguationData":[OSD([subQ0])]})])],"derivedFrom":makeQuery(id+"F1.opExtrude","CAP_FACE",FACE,{"disambiguationData":[OSD([subQ7,subQ6,subQ4,subQ3,subQ2,subQ0,subQ5,subQ1])],"isStart":true})});}
            var sketch = newSketch(context, id + "F29", { "sketchPlane" : qUnion([Q0])});
            skLineSegment(sketch, "E53.bottom", {"start": v(25.25, 0) * mm, "end": v(42.75, 0) * mm});
            skLineSegment(sketch, "E53.top", {"start": v(25.25, -1.5) * mm, "end": v(42.75, -1.5) * mm});
            skLineSegment(sketch, "E53.left", {"start": v(25.25, 0) * mm, "end": v(25.25, -1.5) * mm});
            skLineSegment(sketch, "E53.right", {"start": v(42.75, 0) * mm, "end": v(42.75, -1.5) * mm});
            skLineSegment(sketch, "E54.bottom", {"start": v(7.75, 0) * mm, "end": v(17.25, 0) * mm});
            skLineSegment(sketch, "E54.top", {"start": v(7.75, -1.5) * mm, "end": v(17.25, -1.5) * mm});
            skLineSegment(sketch, "E54.left", {"start": v(7.75, 0) * mm, "end": v(7.75, -1.5) * mm});
            skLineSegment(sketch, "E54.right", {"start": v(17.25, 0) * mm, "end": v(17.25, -1.5) * mm});
            skLineSegment(sketch, "E55.bottom", {"start": v(47.88, 0) * mm, "end": v(62.69, 0) * mm});
            skLineSegment(sketch, "E56.bottom", {"start": v(51.5, 0) * mm, "end": v(59.5, 0) * mm});
            skLineSegment(sketch, "E56.top", {"start": v(51.5, -1.5) * mm, "end": v(59.5, -1.5) * mm});
            skLineSegment(sketch, "E56.left", {"start": v(51.5, 0) * mm, "end": v(51.5, -1.5) * mm});
            skLineSegment(sketch, "E56.right", {"start": v(59.5, 0) * mm, "end": v(59.5, -1.5) * mm});
            skSolve(sketch);
        }
        {
            var Q0;
            Q0=makeQuery(id+"F29.imprint","IMPRINT",FACE,{"disambiguationData":[TD([[makeQuery(id+"F29.imprint","IMPRINT",EDGE,{"derivedFrom":sQuery(id+"F29.wireOp",EDGE,"E53.bottom")}),-1.0]])]});
            var Q1;
            Q1=makeQuery(id+"F29.imprint","IMPRINT",FACE,{"disambiguationData":[TD([[makeQuery(id+"F29.imprint","IMPRINT",EDGE,{"derivedFrom":sQuery(id+"F29.wireOp",EDGE,"E56.bottom")}),1.0]])]});
            extrude(context, id + "F30", {"entities" : qUnion([Q0, Q1]), "operationType" : NewBodyOperationType.ADD, "depth" : 10 * mm});
        }
        {
            var Q0;
            Q0=makeQuery(id+"F29.imprint","IMPRINT",FACE,{"disambiguationData":[TD([[makeQuery(id+"F29.imprint","IMPRINT",EDGE,{"derivedFrom":sQuery(id+"F29.wireOp",EDGE,"E54.bottom")}),-1.0]])]});
            extrude(context, id + "F31", {"entities" : qUnion([Q0]), "operationType" : NewBodyOperationType.ADD, "depth" : 13.5 * mm});
        }
        {
            var Q0;
            Q0=makeQuery(id+"F29.imprint","IMPRINT",FACE,{"disambiguationData":[TD([[makeQuery(id+"F29.imprint","IMPRINT",EDGE,{"derivedFrom":sQuery(id+"F29.wireOp",EDGE,"E53.bottom")}),1.0]])]});
            var sketch = newSketch(context, id + "F32", { "sketchPlane" : qUnion([Q0])});
            skLineSegment(sketch, "E57.0", {"start": v(7.75, -1.5) * mm, "end": v(17.25, -1.5) * mm});
            skLineSegment(sketch, "E58.bottom", {"start": v(11.75, -1.5) * mm, "end": v(13.25, -1.5) * mm});
            skLineSegment(sketch, "E58.top", {"start": v(11.75, -5.5) * mm, "end": v(13.25, -5.5) * mm});
            skLineSegment(sketch, "E58.left", {"start": v(11.75, -1.5) * mm, "end": v(11.75, -5.5) * mm});
            skLineSegment(sketch, "E58.right", {"start": v(13.25, -1.5) * mm, "end": v(13.25, -5.5) * mm});
            skPoint(sketch, "E59", {"position": v(12.5, -1.5) * mm});
            skLineSegment(sketch, "E60.bottom", {"start": v(33.25, -1.5) * mm, "end": v(34.75, -1.5) * mm});
            skLineSegment(sketch, "E60.top", {"start": v(33.25, -5.5) * mm, "end": v(34.75, -5.5) * mm});
            skLineSegment(sketch, "E60.left", {"start": v(33.25, -1.5) * mm, "end": v(33.25, -5.5) * mm});
            skLineSegment(sketch, "E60.right", {"start": v(34.75, -1.5) * mm, "end": v(34.75, -5.5) * mm});
            skLineSegment(sketch, "E61.bottom", {"start": v(54.75, -1.5) * mm, "end": v(56.25, -1.5) * mm});
            skLineSegment(sketch, "E61.top", {"start": v(54.75, -5.5) * mm, "end": v(56.25, -5.5) * mm});
            skLineSegment(sketch, "E61.left", {"start": v(54.75, -1.5) * mm, "end": v(54.75, -5.5) * mm});
            skLineSegment(sketch, "E61.right", {"start": v(56.25, -1.5) * mm, "end": v(56.25, -5.5) * mm});
            skSolve(sketch);
        }
        {
            var Q0;
            Q0=makeQuery(id+"F32.imprint","IMPRINT",FACE,{"disambiguationData":[TD([[makeQuery(id+"F32.imprint","IMPRINT",EDGE,{"derivedFrom":sQuery(id+"F32.wireOp",EDGE,"E60.bottom")}),-1.0]])]});
            var Q1;
            Q1=makeQuery(id+"F32.imprint","IMPRINT",FACE,{"disambiguationData":[TD([[makeQuery(id+"F32.imprint","IMPRINT",EDGE,{"derivedFrom":sQuery(id+"F32.wireOp",EDGE,"E61.bottom")}),-1.0]])]});
            var Q2;
            Q2=makeQuery(id+"F32.imprint","IMPRINT",FACE,{"disambiguationData":[TD([[makeQuery(id+"F32.imprint","IMPRINT",EDGE,{"derivedFrom":sQuery(id+"F32.wireOp",EDGE,"E58.bottom")}),-1.0]])]});
            extrude(context, id + "F33", {"entities" : qUnion([Q0, Q1, Q2]), "operationType" : NewBodyOperationType.ADD, "depth" : 4 * mm});
        }
        {
            var Q0;
            Q0=makeQuery(id+"F33.opExtrude","CAP_EDGE",EDGE,{"disambiguationData":[OSD([sQuery(id+"F32.wireOp",EDGE,"E58.top")])],"isStart":false});
            var Q1;
            Q1=makeQuery(id+"F33.opExtrude","CAP_EDGE",EDGE,{"disambiguationData":[OSD([sQuery(id+"F32.wireOp",EDGE,"E60.top")])],"isStart":false});
            var Q2;
            Q2=makeQuery(id+"F33.opExtrude","CAP_EDGE",EDGE,{"disambiguationData":[OSD([sQuery(id+"F32.wireOp",EDGE,"E61.top")])],"isStart":false});
            chamfer(context, id + "F34", {"entities" : qUnion([Q0, Q1, Q2]), "width" : 4 * mm, "tangentPropagation" : true});
        }
        {
            var Q0;
            Q0=makeQuery(id+"F1.opExtrude","CAP_FACE",FACE,{"disambiguationData":[OSD([sQuery(id+"F0.wireOp",EDGE,"E2"),sQuery(id+"F0.wireOp",EDGE,"E3"),sQuery(id+"F0.wireOp",EDGE,"E4"),sQuery(id+"F0.wireOp",EDGE,"E5"),sQuery(id+"F0.wireOp",EDGE,"E6"),sQuery(id+"F0.wireOp",EDGE,"E8.top"),sQuery(id+"F0.wireOp",EDGE,"E8.left"),sQuery(id+"F0.wireOp",EDGE,"E8.right")])],"isStart":false});
            var sketch = newSketch(context, id + "F35", { "sketchPlane" : qUnion([Q0])});
            skPoint(sketch, "E62.0", {"position": v(28.9, 20.75) * mm});
            skArc(sketch, "E63", {"start": v(32.32, 4) * mm, "mid": v(32.76, 3.26) * mm, "end": v(33.5, 2.82) * mm});
            skLineSegment(sketch, "E64.bottom", {"start": v(37, 5) * mm, "end": v(35.68, 5) * mm});
            skLineSegment(sketch, "E64.top", {"start": v(37, 4) * mm, "end": v(35.68, 4) * mm});
            skLineSegment(sketch, "E64.left", {"start": v(37, 5) * mm, "end": v(37, 4) * mm});
            skLineSegment(sketch, "E64.right", {"start": v(31, 5) * mm, "end": v(31, 4) * mm});
            skLineSegment(sketch, "E65.bottom", {"start": v(34.5, 7.5) * mm, "end": v(33.5, 7.5) * mm});
            skLineSegment(sketch, "E65.top", {"start": v(34.5, 1.5) * mm, "end": v(33.5, 1.5) * mm});
            skLineSegment(sketch, "E65.left", {"start": v(34.5, 7.5) * mm, "end": v(34.5, 6.18) * mm});
            skLineSegment(sketch, "E65.right", {"start": v(33.5, 7.5) * mm, "end": v(33.5, 6.18) * mm});
            skLineSegment(sketch, "E66.trimOffspring", {"start": v(32.32, 5) * mm, "end": v(31, 5) * mm});
            skLineSegment(sketch, "E67.trimOffspring", {"start": v(32.32, 4) * mm, "end": v(31, 4) * mm});
            skLineSegment(sketch, "E68.trimOffspring", {"start": v(33.5, 2.82) * mm, "end": v(33.5, 1.5) * mm});
            skLineSegment(sketch, "E69.trimOffspring", {"start": v(34.5, 2.82) * mm, "end": v(34.5, 1.5) * mm});
            skArc(sketch, "E70.trimOffspring", {"start": v(33.5, 6.18) * mm, "mid": v(32.76, 5.74) * mm, "end": v(32.32, 5) * mm});
            skArc(sketch, "E71.trimOffspring", {"start": v(35.68, 5) * mm, "mid": v(35.24, 5.74) * mm, "end": v(34.5, 6.18) * mm});
            skArc(sketch, "E72.trimOffspring", {"start": v(34.5, 2.82) * mm, "mid": v(35.24, 3.26) * mm, "end": v(35.68, 4) * mm});
            skCircle(sketch, "E73", {"center": v(34, 4.5) * mm, "radius": 1 * mm});
            skArc(sketch, "E74", {"start": v(63.82, 20.25) * mm, "mid": v(64.26, 19.51) * mm, "end": v(65, 19.07) * mm});
            skLineSegment(sketch, "E75.bottom", {"start": v(68.5, 21.25) * mm, "end": v(67.18, 21.25) * mm});
            skLineSegment(sketch, "E75.top", {"start": v(68.5, 20.25) * mm, "end": v(67.18, 20.25) * mm});
            skLineSegment(sketch, "E75.left", {"start": v(68.5, 21.25) * mm, "end": v(68.5, 20.25) * mm});
            skLineSegment(sketch, "E75.right", {"start": v(62.5, 21.25) * mm, "end": v(62.5, 20.25) * mm});
            skLineSegment(sketch, "E76.bottom", {"start": v(66, 23.75) * mm, "end": v(65, 23.75) * mm});
            skLineSegment(sketch, "E76.top", {"start": v(66, 17.75) * mm, "end": v(65, 17.75) * mm});
            skLineSegment(sketch, "E76.left", {"start": v(66, 23.75) * mm, "end": v(66, 22.43) * mm});
            skLineSegment(sketch, "E76.right", {"start": v(65, 23.75) * mm, "end": v(65, 22.43) * mm});
            skLineSegment(sketch, "E77.trimOffspring", {"start": v(63.82, 21.25) * mm, "end": v(62.5, 21.25) * mm});
            skLineSegment(sketch, "E78.trimOffspring", {"start": v(63.82, 20.25) * mm, "end": v(62.5, 20.25) * mm});
            skLineSegment(sketch, "E79.trimOffspring", {"start": v(65, 19.07) * mm, "end": v(65, 17.75) * mm});
            skLineSegment(sketch, "E80.trimOffspring", {"start": v(66, 19.07) * mm, "end": v(66, 17.75) * mm});
            skArc(sketch, "E81.trimOffspring", {"start": v(65, 22.43) * mm, "mid": v(64.26, 21.99) * mm, "end": v(63.82, 21.25) * mm});
            skArc(sketch, "E82.trimOffspring", {"start": v(67.18, 21.25) * mm, "mid": v(66.74, 21.99) * mm, "end": v(66, 22.43) * mm});
            skArc(sketch, "E83.trimOffspring", {"start": v(66, 19.07) * mm, "mid": v(66.74, 19.51) * mm, "end": v(67.18, 20.25) * mm});
            skCircle(sketch, "E84", {"center": v(65.5, 20.75) * mm, "radius": 1 * mm});
            skLineSegment(sketch, "E85", {"start": v(65.5, 20.75) * mm, "end": v(65.5, -20) * mm});
            skLineSegment(sketch, "E86", {"start": v(65.5, 20.75) * mm, "end": v(65.5, 61.5) * mm});
            skSolve(sketch);
        }
        {
            var Q0;
            Q0=makeQuery(id+"F35.imprint","IMPRINT",FACE,{"disambiguationData":[TD([[makeQuery(id+"F35.imprint","IMPRINT",EDGE,{"derivedFrom":sQuery(id+"F35.wireOp",EDGE,"E63")}),1.0]])]});
            var Q1;
            Q1=makeQuery(id+"F35.imprint","IMPRINT",FACE,{"disambiguationData":[TD([[makeQuery(id+"F35.imprint","IMPRINT",EDGE,{"derivedFrom":sQuery(id+"F35.wireOp",EDGE,"E74")}),1.0]])]});
            var Q2;
            Q2=makeQuery(id+"F35.imprint","IMPRINT",FACE,{"disambiguationData":[TD([[makeQuery(id+"F35.imprint","IMPRINT",EDGE,{"derivedFrom":sQuery(id+"F35.wireOp",EDGE,"E75.bottom")}),1.0]])]});
            extrude(context, id + "F36", {"entities" : qUnion([Q0, Q1, Q2]), "operationType" : NewBodyOperationType.ADD, "endBound" : BoundingType.UP_TO_NEXT, "depth" : 25 * mm});
        }
        {
            var Q0;
            {var subQ0=sQuery(id+"F0.wireOp",EDGE,"E8.top");var subQ1=sQuery(id+"F0.wireOp",EDGE,"E8.right");var subQ2=sQuery(id+"F0.wireOp",EDGE,"E6");var subQ3=sQuery(id+"F0.wireOp",EDGE,"E5");var subQ4=sQuery(id+"F0.wireOp",EDGE,"E4");var subQ5=sQuery(id+"F0.wireOp",EDGE,"E8.left");var subQ6=sQuery(id+"F0.wireOp",EDGE,"E3");var subQ7=sQuery(id+"F0.wireOp",EDGE,"E2");Q0=makeQuery(id+"F3.boolean.opBoolean","SPLIT",FACE,{"disambiguationData":[TD([makeQuery(id+"F1.opExtrude","SWEPT_FACE",FACE,{"disambiguationData":[OSD([subQ0])]})])],"derivedFrom":makeQuery(id+"F1.opExtrude","CAP_FACE",FACE,{"disambiguationData":[OSD([subQ7,subQ6,subQ4,subQ3,subQ2,subQ0,subQ5,subQ1])],"isStart":true})});}
            var sketch = newSketch(context, id + "F37", { "sketchPlane" : qUnion([Q0])});
            skLineSegment(sketch, "E87.bottom", {"start": v(60.5, -44.5) * mm, "end": v(85.5, -44.5) * mm});
            skLineSegment(sketch, "E87.top", {"start": v(60.5, -24.5) * mm, "end": v(85.5, -24.5) * mm});
            skLineSegment(sketch, "E87.left", {"start": v(60.5, -44.5) * mm, "end": v(60.5, -24.5) * mm});
            skLineSegment(sketch, "E87.right", {"start": v(85.5, -44.5) * mm, "end": v(85.5, -24.5) * mm});
            skCircle(sketch, "E88.0", {"center": v(65.5, -20.75) * mm, "radius": 1 * mm});
            skCircle(sketch, "E89.0", {"center": v(63.5, -54.5) * mm, "radius": 1.5 * mm});
            skPoint(sketch, "E90.endSnap0", {"position": v(60.5, -34.5) * mm});
            skSolve(sketch);
        }
        {
            var Q0;
            {var subQ5=sQuery(id+"F37.wireOp",EDGE,"E87.left");Q0=makeQuery(id+"F37.imprint","IMPRINT",FACE,{"disambiguationData":[TD([[makeQuery(id+"F37.imprint","IMPRINT",EDGE,{"derivedFrom":subQ5}),-1.0]])]});}
            var Q1;
            {var subQ1=sQuery(id+"F0.wireOp",EDGE,"E8.top");var subQ2=sQuery(id+"F0.wireOp",EDGE,"E5");var subQ3=sQuery(id+"F0.wireOp",EDGE,"E4");Q1=makeQuery(id+"F36.boolean.opBoolean","SPLIT",FACE,{"disambiguationData":[TD([makeQuery(id+"F5.boolean.opBoolean","COPY",FACE,{"derivedFrom":makeQuery(id+"F5.opExtrude","SWEPT_FACE",FACE,{"disambiguationData":[OSD([sQuery(id+"F4.wireOp",EDGE,"E12.bottom")])]})})])],"derivedFrom":makeQuery(id+"F1.opExtrude","CAP_FACE",FACE,{"disambiguationData":[OSD([sQuery(id+"F0.wireOp",EDGE,"E2"),sQuery(id+"F0.wireOp",EDGE,"E3"),subQ3,subQ2,sQuery(id+"F0.wireOp",EDGE,"E6"),subQ1,sQuery(id+"F0.wireOp",EDGE,"E8.left"),sQuery(id+"F0.wireOp",EDGE,"E8.right")])],"isStart":false})});}
            extrude(context, id + "F38", {"entities" : qUnion([Q0]), "operationType" : NewBodyOperationType.REMOVE, "endBound" : BoundingType.UP_TO_SURFACE, "oppositeDirection" : true, "endBoundEntityFace" : qUnion([Q1]), "depth" : 25 * mm});
        }
        {
            var Q0;
            {var subQ0=sQuery(id+"F6.wireOp",EDGE,"E14.right");Q0=makeQuery(id+"F36.boolean.opBoolean","SPLIT",FACE,{"disambiguationData":[TD([makeQuery(id+"F7.opExtrude","SWEPT_FACE",FACE,{"disambiguationData":[OSD([subQ0])]})])],"derivedFrom":makeQuery(id+"F17.opExtrude","SWEPT_FACE",FACE,{"disambiguationData":[OSD([sQuery(id+"F16.wireOp",EDGE,"E24")])]})});}
            var sketch = newSketch(context, id + "F39", { "sketchPlane" : qUnion([Q0])});
            skLineSegment(sketch, "E91.bottom", {"start": v(89.5, -30.75) * mm, "end": v(83.5, -30.75) * mm});
            skLineSegment(sketch, "E91.top", {"start": v(89.5, -36.75) * mm, "end": v(83.5, -36.75) * mm});
            skLineSegment(sketch, "E91.left", {"start": v(89.5, -30.75) * mm, "end": v(89.5, -36.75) * mm});
            skLineSegment(sketch, "E91.right", {"start": v(83.5, -30.75) * mm, "end": v(83.5, -36.75) * mm});
            skPoint(sketch, "E91.middle", {"position": v(86.5, -33.75) * mm});
            skArc(sketch, "E92.0", {"start": v(85.25, -28.75) * mm, "mid": v(84, -30) * mm, "end": v(82.75, -28.75) * mm});
            skArc(sketch, "E93.0", {"start": v(90.25, -28.75) * mm, "mid": v(89, -30) * mm, "end": v(87.75, -28.75) * mm});
            skLineSegment(sketch, "E94", {"start": v(86.5, -33.75) * mm, "end": v(84, -28.75) * mm});
            skLineSegment(sketch, "E95", {"start": v(86.5, -33.75) * mm, "end": v(89, -28.75) * mm});
            skLineSegment(sketch, "E96.bottom", {"start": v(89.5, -10.75) * mm, "end": v(83.5, -10.75) * mm});
            skLineSegment(sketch, "E96.top", {"start": v(89.5, -4.75) * mm, "end": v(83.5, -4.75) * mm});
            skLineSegment(sketch, "E96.left", {"start": v(89.5, -10.75) * mm, "end": v(89.5, -4.75) * mm});
            skLineSegment(sketch, "E96.right", {"start": v(83.5, -10.75) * mm, "end": v(83.5, -4.75) * mm});
            skPoint(sketch, "E96.middle", {"position": v(86.5, -7.75) * mm});
            skArc(sketch, "E97.0", {"start": v(87.75, -12.75) * mm, "mid": v(89, -11.5) * mm, "end": v(90.25, -12.75) * mm});
            skSolve(sketch);
        }
        {
            var Q0;
            Q0=makeQuery(id+"F39.imprint","IMPRINT",FACE,{"disambiguationData":[TD([[makeQuery(id+"F39.imprint","IMPRINT",EDGE,{"derivedFrom":sQuery(id+"F39.wireOp",EDGE,"E91.top")}),-1.0]])]});
            var Q1;
            {var subQ0=sQuery(id+"F39.wireOp",EDGE,"E95");var subQ1=sQuery(id+"F39.wireOp",EDGE,"E91.bottom");var subQ2=makeQuery(id+"F39.imprint","INTERSECT",VERTEX,{"derivedFrom":[subQ1,subQ0]});Q1=makeQuery(id+"F39.imprint","IMPRINT",FACE,{"disambiguationData":[TD([[makeQuery(id+"F39.imprint","IMPRINT",EDGE,{"disambiguationData":[TD([[subQ2,-1.0]])],"derivedFrom":subQ1}),1.0]])]});}
            var Q2;
            Q2=makeQuery(id+"F39.imprint","IMPRINT",FACE,{"disambiguationData":[TD([[makeQuery(id+"F39.imprint","IMPRINT",EDGE,{"derivedFrom":sQuery(id+"F39.wireOp",EDGE,"E96.bottom")}),-1.0]])]});
            extrude(context, id + "F40", {"entities" : qUnion([Q0, Q1, Q2]), "operationType" : NewBodyOperationType.ADD, "depth" : 4 * mm});
        }
        {
            var Q0;
            {var subQ0=sQuery(id+"F0.wireOp",EDGE,"E8.top");var subQ1=sQuery(id+"F0.wireOp",EDGE,"E8.right");var subQ2=sQuery(id+"F0.wireOp",EDGE,"E6");var subQ3=sQuery(id+"F0.wireOp",EDGE,"E5");var subQ4=sQuery(id+"F0.wireOp",EDGE,"E4");var subQ5=sQuery(id+"F0.wireOp",EDGE,"E8.left");var subQ6=sQuery(id+"F0.wireOp",EDGE,"E3");var subQ7=sQuery(id+"F0.wireOp",EDGE,"E2");Q0=makeQuery(id+"F3.boolean.opBoolean","SPLIT",FACE,{"disambiguationData":[TD([makeQuery(id+"F1.opExtrude","SWEPT_FACE",FACE,{"disambiguationData":[OSD([subQ0])]})])],"derivedFrom":makeQuery(id+"F1.opExtrude","CAP_FACE",FACE,{"disambiguationData":[OSD([subQ7,subQ6,subQ4,subQ3,subQ2,subQ0,subQ5,subQ1])],"isStart":true})});}
            var sketch = newSketch(context, id + "F41", { "sketchPlane" : qUnion([Q0])});
            skLineSegment(sketch, "E98.0.0", {"start": v(102, 20) * mm, "end": v(-13, 20) * mm});
            skArc(sketch, "E98.0.1", {"start": v(-13, 20) * mm, "mid": v(-14.41, 19.41) * mm, "end": v(-15, 18) * mm});
            skLineSegment(sketch, "E98.0.2", {"start": v(-15, 18) * mm, "end": v(-15, -59.5) * mm});
            skArc(sketch, "E98.0.3", {"start": v(-15, -59.5) * mm, "mid": v(-14.41, -60.91) * mm, "end": v(-13, -61.5) * mm});
            skLineSegment(sketch, "E98.0.4", {"start": v(-13, -61.5) * mm, "end": v(102, -61.5) * mm});
            skArc(sketch, "E98.0.5", {"start": v(102, -61.5) * mm, "mid": v(103.41, -60.91) * mm, "end": v(104, -59.5) * mm});
            skLineSegment(sketch, "E98.0.6", {"start": v(104, -59.5) * mm, "end": v(104, 18) * mm});
            skArc(sketch, "E98.0.7", {"start": v(104, 18) * mm, "mid": v(103.41, 19.41) * mm, "end": v(102, 20) * mm});
            skLineSegment(sketch, "E99.bottom", {"start": v(68.5, -21.5) * mm, "end": v(85.5, -21.5) * mm});
            skLineSegment(sketch, "E99.top", {"start": v(68.5, -5) * mm, "end": v(85.5, -5) * mm});
            skLineSegment(sketch, "E99.left", {"start": v(68.5, -21.5) * mm, "end": v(68.5, -5) * mm});
            skLineSegment(sketch, "E99.right", {"start": v(85.5, -21.5) * mm, "end": v(85.5, -5) * mm});
            skLineSegment(sketch, "E100.bottom", {"start": v(68.5, -48) * mm, "end": v(85.5, -48) * mm});
            skLineSegment(sketch, "E100.top", {"start": v(68.5, -56.5) * mm, "end": v(85.5, -56.5) * mm});
            skLineSegment(sketch, "E100.left", {"start": v(68.5, -48) * mm, "end": v(68.5, -56.5) * mm});
            skLineSegment(sketch, "E100.right", {"start": v(85.5, -48) * mm, "end": v(85.5, -56.5) * mm});
            skLineSegment(sketch, "E101.bottom", {"start": v(62.69, 20) * mm, "end": v(104, 20) * mm});
            skLineSegment(sketch, "E101.top", {"start": v(62.69, -1.5) * mm, "end": v(104, -1.5) * mm});
            skLineSegment(sketch, "E101.left", {"start": v(62.69, 20) * mm, "end": v(62.69, -1.5) * mm});
            skLineSegment(sketch, "E101.right", {"start": v(104, 20) * mm, "end": v(104, -1.5) * mm});
            skLineSegment(sketch, "E102.bottom", {"start": v(66.19, 16.5) * mm, "end": v(100.5, 16.5) * mm});
            skLineSegment(sketch, "E102.top", {"start": v(66.19, 2) * mm, "end": v(100.5, 2) * mm});
            skLineSegment(sketch, "E102.left", {"start": v(66.19, 16.5) * mm, "end": v(66.19, 2) * mm});
            skLineSegment(sketch, "E102.right", {"start": v(100.5, 16.5) * mm, "end": v(100.5, 2) * mm});
            skSolve(sketch);
        }
        {
            var Q0;
            Q0=makeQuery(id+"F41.imprint","IMPRINT",FACE,{"disambiguationData":[TD([[makeQuery(id+"F41.imprint","IMPRINT",EDGE,{"derivedFrom":sQuery(id+"F41.wireOp",EDGE,"E99.bottom")}),1.0]])]});
            var Q1;
            Q1=makeQuery(id+"F41.imprint","IMPRINT",FACE,{"disambiguationData":[TD([[makeQuery(id+"F41.imprint","IMPRINT",EDGE,{"derivedFrom":sQuery(id+"F41.wireOp",EDGE,"E102.bottom")}),-1.0]])]});
            var Q2;
            Q2=makeQuery(id+"F41.imprint","IMPRINT",FACE,{"disambiguationData":[TD([[makeQuery(id+"F41.imprint","IMPRINT",EDGE,{"derivedFrom":sQuery(id+"F41.wireOp",EDGE,"E100.bottom")}),-1.0]])]});
            var Q3;
            {var subQ1=sQuery(id+"F0.wireOp",EDGE,"E8.top");var subQ2=sQuery(id+"F0.wireOp",EDGE,"E5");var subQ3=sQuery(id+"F0.wireOp",EDGE,"E4");Q3=makeQuery(id+"F36.boolean.opBoolean","SPLIT",FACE,{"disambiguationData":[TD([makeQuery(id+"F5.boolean.opBoolean","COPY",FACE,{"derivedFrom":makeQuery(id+"F5.opExtrude","SWEPT_FACE",FACE,{"disambiguationData":[OSD([sQuery(id+"F4.wireOp",EDGE,"E12.bottom")])]})})])],"derivedFrom":makeQuery(id+"F1.opExtrude","CAP_FACE",FACE,{"disambiguationData":[OSD([sQuery(id+"F0.wireOp",EDGE,"E2"),sQuery(id+"F0.wireOp",EDGE,"E3"),subQ3,subQ2,sQuery(id+"F0.wireOp",EDGE,"E6"),subQ1,sQuery(id+"F0.wireOp",EDGE,"E8.left"),sQuery(id+"F0.wireOp",EDGE,"E8.right")])],"isStart":false})});}
            extrude(context, id + "F42", {"entities" : qUnion([Q0, Q1, Q2]), "operationType" : NewBodyOperationType.REMOVE, "endBound" : BoundingType.UP_TO_SURFACE, "oppositeDirection" : true, "endBoundEntityFace" : qUnion([Q3]), "depth" : 25 * mm});
        }
        {
            var Q0;
            Q0=makeQuery(id+"F0.imprint","IMPRINT",FACE,{"disambiguationData":[TD([[makeQuery(id+"F0.imprint","IMPRINT",EDGE,{"derivedFrom":sQuery(id+"F0.wireOp",EDGE,"E0.bottom")}),-1.0]])]});
            var sketch = newSketch(context, id + "F43", { "sketchPlane" : qUnion([Q0])});
            skLineSegment(sketch, "E103.bottom", {"start": v(-11.5, 56.5) * mm, "end": v(-2, 56.5) * mm});
            skLineSegment(sketch, "E103.top", {"start": v(-11.5, 41) * mm, "end": v(-2, 41) * mm});
            skLineSegment(sketch, "E103.left", {"start": v(-11.5, 56.5) * mm, "end": v(-11.5, 41) * mm});
            skLineSegment(sketch, "E103.right", {"start": v(-2, 56.5) * mm, "end": v(-2, 41) * mm});
            skLineSegment(sketch, "E104.bottom", {"start": v(-11.5, 19) * mm, "end": v(-2, 19) * mm});
            skLineSegment(sketch, "E104.top", {"start": v(-11.5, 2) * mm, "end": v(-2, 2) * mm});
            skLineSegment(sketch, "E104.left", {"start": v(-11.5, 19) * mm, "end": v(-11.5, 2) * mm});
            skLineSegment(sketch, "E104.right", {"start": v(-2, 19) * mm, "end": v(-2, 2) * mm});
            skLineSegment(sketch, "E105.bottom", {"start": v(1.75, -2) * mm, "end": v(-11.5, -2) * mm});
            skLineSegment(sketch, "E105.top", {"start": v(1.75, -16.5) * mm, "end": v(-11.5, -16.5) * mm});
            skLineSegment(sketch, "E105.left", {"start": v(1.75, -2) * mm, "end": v(1.75, -16.5) * mm});
            skLineSegment(sketch, "E105.right", {"start": v(-11.5, -2) * mm, "end": v(-11.5, -16.5) * mm});
            skSolve(sketch);
        }
        {
            var Q0;
            Q0=makeQuery(id+"F43.imprint","IMPRINT",FACE,{"disambiguationData":[TD([[makeQuery(id+"F43.imprint","IMPRINT",EDGE,{"derivedFrom":sQuery(id+"F43.wireOp",EDGE,"E105.bottom")}),1.0]])]});
            var Q1;
            Q1=makeQuery(id+"F43.imprint","IMPRINT",FACE,{"disambiguationData":[TD([[makeQuery(id+"F43.imprint","IMPRINT",EDGE,{"derivedFrom":sQuery(id+"F43.wireOp",EDGE,"E104.bottom")}),-1.0]])]});
            var Q2;
            Q2=makeQuery(id+"F43.imprint","IMPRINT",FACE,{"disambiguationData":[TD([[makeQuery(id+"F43.imprint","IMPRINT",EDGE,{"derivedFrom":sQuery(id+"F43.wireOp",EDGE,"E103.bottom")}),-1.0]])]});
            extrude(context, id + "F44", {"entities" : qUnion([Q0, Q1, Q2]), "operationType" : NewBodyOperationType.REMOVE, "endBound" : BoundingType.UP_TO_NEXT, "depth" : 25 * mm});
        }
    });
